# Revit family: PRD_FrankeWS_ShwrEnclsrs_HousingExtension_ZSHOW0008-ZSHOW0011
name_source: partatom
category: Specialty Equipment
revit_build: Autodesk Revit 2018 (Build: 20190510_1515(x64)
units: mm (PartAtom-declared; Revit-internal decimal feet)

## family parameters
Cut with Voids When Loaded = No
Host = Face
OmniClass Number = 23.45.05.14.17.11
OmniClass Title = Shower Compartments
Part Type = Normal
Room Calculation Point = No
Round Connector Dimension = Use Diameter
Shared = No

## types (4) — shared parameters
AssetType = Fixed
CasingMaterial = PRD_AR_StainlessSteel_AlpineWhite
Category = Pr_40_20_06_79, Shower enclosures
Color = white
Default Elevation = 1500 mm  [stored 4.92126 ft]
Description = Housing extension made of stainless steel for shower panel SMARTWAVE, white (RAL 9010) powder coated, with height-adjustment, for cladding of surface pipe installations, fixing set included.
DurationUnit = year
Finish = Powder coat galvanized
IfcExportAs = IfcSanitaryTerminalType
IfcExportType = USERDEFINED
IntegralAccessories = fixing set included
IsBuiltIn = TRUE
MainColor = stainless steel
Manufacturer = KWC Group AG
ManufacturerName = KWC Group AG
ManufacturerURL = www.kwc.com
Material = stainless steel
MaterialCode = 1.4301 Chrome Nickel steel V2A
NBSDescription = Shower enclosures
NBSReference = 45-35-70/332
NominalDepth = 68 mm
NominalWidth = 104 mm
ProductInformation = https://pim.kwc.com
SurfaceTreatment = Coated
TailorMade = No
TypeOfExtension = Shower panel Smartwave
URL = www.kwc.com
Uniclass2015Code = Pr_40_20_06_79
Uniclass2015Title = Shower enclosures
Uniclass2015Version = Products v1.23
Version = 1
WarrantyDurationUnit = year

## per-type parameters (varying)
| type | BIMObjectName | Features | GrossWeight | HeightMax | HeightMiddle | HeightMin | ModelNumber | Name | NetWeight | NominalHeight | NominalLength | ProductCode | Size |
| ZSHOW0008 | PRD_AR_ShowerEnclosures_HousingExtension_ZSHOW0008 | for shower panel SMARTWAVE, with height-adjustment 105 - 165 mm | 0.53 kg | 165 mm | 150 mm | 105 mm  [stored 0.344488 ft] | 2000111076 | Housing Extension ZSHOW0008 | 0.51 kg | 165 mm | 165 mm | 210.0636.664 | 104 x 105-165 x 68 mm (W x H x D) |
| ZSHOW0009 | PRD_AR_ShowerEnclosures_HousingExtension_ZSHOW0009 | for shower panel SMARTWAVE, with height-adjustment 155 - 260 mm | 0.00 kg | 260 mm  [stored 0.853018 ft] | 245 mm  [stored 0.803806 ft] | 155 mm  [stored 0.50853 ft] | 2000111077 | Housing Extension ZSHOW0009 | 0.00 kg | 260 mm  [stored 0.853018 ft] | 260 mm  [stored 0.853018 ft] | 210.0636.665 | 104 x 155-260 x 68 mm (W x H x D) |
| ZSHOW0010 | PRD_AR_ShowerEnclosures_HousingExtension_ZSHOW0010 | for shower panel SMARTWAVE, with height-adjustment 250 - 360 mm | 1.10 kg | 360 mm  [stored 1.1811 ft] | 345 mm  [stored 1.13189 ft] | 250 mm  [stored 0.82021 ft] | 2000111078 | Housing Extension ZSHOW0010 | 1.05 kg | 360 mm  [stored 1.1811 ft] | 360 mm  [stored 1.1811 ft] | 210.0636.666 | 104 x 250-360 x 68 mm (W x H x D) |
| ZSHOW0011 | PRD_AR_ShowerEnclosures_HousingExtension_ZSHOW0011 | for shower panel SMARTWAVE, with height-adjustment 350 - 460 mm | 1.24 kg | 460 mm  [stored 1.50919 ft] | 445 mm  [stored 1.45997 ft] | 350 mm  [stored 1.14829 ft] | 2000111079 | Housing Extension ZSHOW0011 | 1.20 kg | 460 mm  [stored 1.50919 ft] | 460 mm  [stored 1.50919 ft] | 210.0636.667 | 104 x 350-460 x 68 mm (W x H x D) |

note: column(s) folded — value = type name in every type: Model, ModelReference

note: [stored X ft] marks values corroborated as IEEE doubles in the binary element streams (Revit-internal decimal feet)

## geometry (parser evidence)
native form markers: Sweep x2
no freeform markers — native parametric forms only
